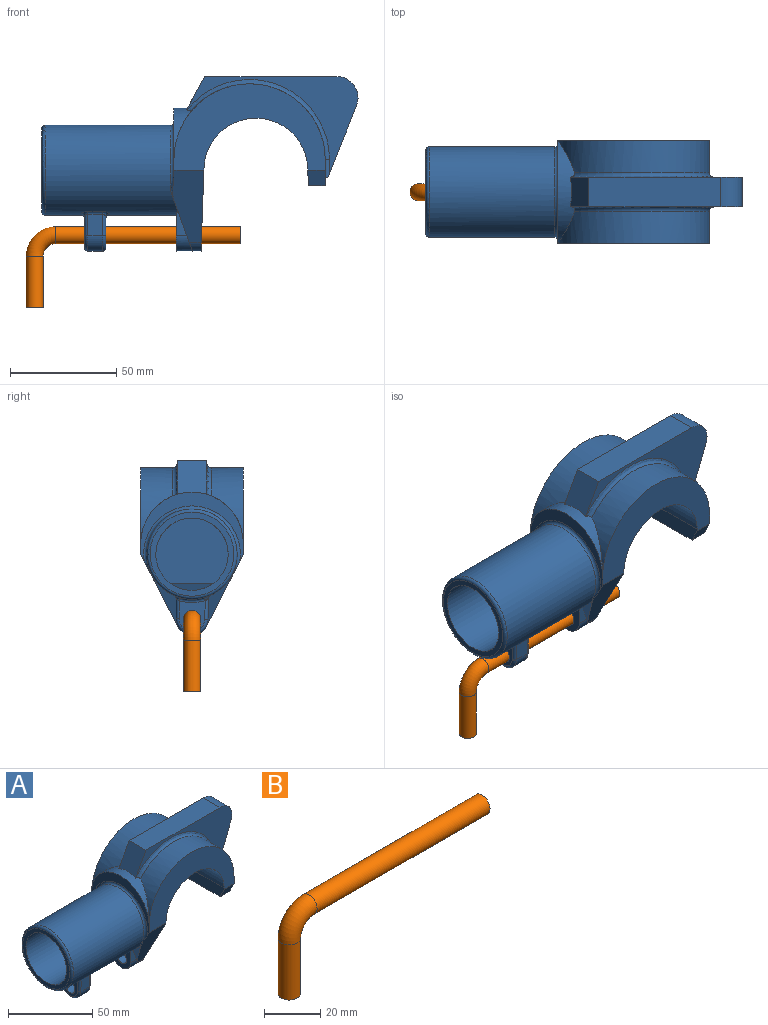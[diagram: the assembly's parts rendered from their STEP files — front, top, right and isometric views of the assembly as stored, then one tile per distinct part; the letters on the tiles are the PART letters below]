
ASSEMBLY  parts=2 mates=1
PART A: 63 faces, bbox 148.7x49.3x86 mm
  f0: cylinder r=21.2mm len=62.62mm, axis (1,0,0), area 7740.6mm2, adj f1,f2,f41,f43,f44,f46,f47,f49
  f1: plane 24.1x12.21mm, normal (-0.94,0,-0.34), area 61.4mm2, adj f0,f15,f54,f58,f60
  f2: plane 28.33x18.79mm, normal (-0.94,0,-0.34), area 63.1mm2, adj f0,f14,f16,f54,f59,f60
  f3: cylinder r=35.53mm len=71.06mm, axis (0,1,0), area 1428.5mm2, adj f5,f12,f27,f29
  f4: cylinder r=35.53mm len=71.06mm, axis (0,1,0), area 1428.5mm2, adj f5,f10,f25,f29
  f5: plane 48.2x12.36mm, normal (1,0,0), area 413.2mm2, adj f3,f4,f9,f10,f12,f13,f17,f18
  f6: plane 48.2x32.34mm, normal (-1,0,0), area 350.6mm2, adj f10,f12,f14,f15,f29,f54
  f7: plane 48.2x38.85mm, normal (1,0,-0.03), area 1125.1mm2, adj f10,f11,f12,f14,f15,f16
  f8: plane 48.2x8.16mm, normal (-1,0,-0.03), area 366.3mm2, adj f9,f10,f11,f12,f13,f17
  f9: plane 40.72x7.92mm, normal (0,0,-1), area 322.5mm2, adj f5,f8,f13,f17
  f10: plane 71.06x40.61mm, normal (0,1,0), area 1407.3mm2, adj f4,f5,f6,f7,f8,f11,f13,f14
  f11: cylinder r=24.4mm len=48.77mm, axis (0,1,0), area 3612.7mm2, adj f7,f8,f10,f12
  f12: plane 71.06x40.61mm, normal (0,-1,0), area 1407.3mm2, adj f3,f5,f6,f7,f8,f11,f15,f17
  f13: plane 8.17x7.28mm, normal (0,0.89,-0.46), area 65.8mm2, adj f5,f8,f9,f10
  f14: plane 33.9x17.43mm, normal (0,0.89,-0.46), area 436.6mm2, adj f2,f6,f7,f10,f16,f54
  f15: plane 33.9x17.43mm, normal (0,-0.89,-0.46), area 436.6mm2, adj f1,f6,f7,f12,f16,f54,f56
  f16: cylinder r=7.5mm len=13.34mm, axis (1,0,0), area 75mm2, adj f2,f7,f14,f15,f56
  f17: plane 8.17x7.28mm, normal (0,-0.89,-0.46), area 65.8mm2, adj f5,f8,f9,f12
  f18: plane 18x1.21mm, normal (0,0,-1), area 18.6mm2, adj f5,f19,f26,f28
  f19: plane 33.92x14.37mm, normal (0.93,0,-0.37), area 510.7mm2, adj f18,f20,f23,f24,f26,f28
  f20: cylinder r=10mm len=14mm, axis (0,1,0), area 273mm2, adj f19,f21,f23,f24
  f21: plane 62x14mm, normal (0,0,1), area 868mm2, adj f20,f22,f23,f24
  f22: plane 15.89x14mm, normal (-0.88,0,0.48), area 242.4mm2, adj f21,f23,f24,f29
  f23: plane 80.68x45.59mm, normal (0,-1,0), area 824.3mm2, adj f19,f20,f21,f22,f27,f28,f29
  f24: plane 80.68x45.59mm, normal (0,1,0), area 824.3mm2, adj f19,f20,f21,f22,f25,f26,f29
  f25: torus R=37.53mm, axis (0,-1,0), area 280.3mm2, adj f4,f24,f26,f29
  f26: cylinder r=2mm len=8.62mm, axis (0,0,-1), area 26.3mm2, adj f5,f18,f19,f24,f25
  f27: torus R=37.53mm, axis (0,-1,0), area 280.3mm2, adj f3,f23,f28,f29
  f28: cylinder r=2mm len=8.62mm, axis (0,0,1), area 26.3mm2, adj f5,f18,f19,f23,f27
  f29: cylinder r=24.1mm len=48.2mm, axis (-1,0,0), area 298.9mm2, adj f3,f4,f6,f22,f23,f24,f25,f27
  f30: cylinder r=17mm len=63.09mm, axis (1,0,0), area 6637.3mm2, adj f31,f32,f33
  f31: plane 39.4x39.4mm, normal (-1,0,0), area 311.3mm2, adj f30,f55
  f32: plane 19.29x3mm, normal (-0.94,0,-0.34), area 41.8mm2, adj f30,f33
  f33: plane 34x31mm, normal (-1,0,0), area 868.6mm2, adj f30,f32
  f34: plane 9.13x7mm, normal (0,1,0), area 63.9mm2, adj f35,f45,f50,f53
  f35: cylinder r=7.5mm len=15mm, axis (1,0,0), area 167.4mm2, adj f34,f37,f42,f51
  f36: cylinder r=4.05mm len=10mm, axis (1,0,0), area 254.5mm2, adj f38,f39
  f37: plane 9.97x7mm, normal (0,-1,-0.02), area 69.8mm2, adj f35,f40,f43,f48
  f38: plane 14.66x12.2mm, normal (-1,0,0), area 102.6mm2, adj f36,f40,f42,f44,f45
  f39: plane 14.66x12.2mm, normal (1,0,0), area 102.6mm2, adj f36,f48,f49,f51,f53
  f40: cylinder r=1.5mm len=10.01mm, axis (0,0.02,-1), area 22.4mm2, adj f37,f38,f41,f42
  f41: bspline ~3.18x2.99mm, area 6.8mm2, adj f0,f40,f43,f44
  f42: torus R=6mm, axis (-1,0,0), area 52.3mm2, adj f35,f38,f40,f45
  f43: cylinder r=1.5mm len=7mm, axis (1,0,0), area 11.9mm2, adj f0,f37,f41,f46
  f44: torus R=22.7mm, axis (-1,0,0), area 27.8mm2, adj f0,f38,f41,f47
  f45: cylinder r=1.5mm len=9.19mm, axis (0,0,1), area 20.6mm2, adj f34,f38,f42,f47
  f46: bspline ~3.62x3.18mm, area 6.8mm2, adj f0,f43,f48,f49
  f47: bspline ~3.62x3.17mm, area 6.8mm2, adj f0,f44,f45,f50
  f48: cylinder r=1.5mm len=10.01mm, axis (0,-0.02,1), area 22.4mm2, adj f37,f39,f46,f51
  f49: torus R=22.7mm, axis (-1,0,0), area 27.8mm2, adj f0,f39,f46,f52
  f50: cylinder r=1.5mm len=7mm, axis (1,0,0), area 12.2mm2, adj f0,f34,f47,f52
  f51: torus R=6mm, axis (-1,0,0), area 52.3mm2, adj f35,f39,f48,f53
  f52: bspline ~3.62x3.44mm, area 6.8mm2, adj f0,f49,f50,f53
  f53: cylinder r=1.5mm len=9.19mm, axis (0,0,-1), area 20.6mm2, adj f34,f39,f51,f52
  f54: torus R=22.7mm, axis (1,0,0), area 198.7mm2, adj f0,f1,f2,f6,f14,f15
  f55: torus R=19.7mm, axis (-1,0,0), area 305.8mm2, adj f0,f31
  f56: plane 6.93x4.23mm, normal (0.94,0,0.34), area 0mm2, adj f15,f16,f60
  f57: plane 18.27x15.25mm, normal (-1,0,0), area 184.3mm2, adj f0,f58,f59,f60,f61
  f58: plane 10.94x5.06mm, normal (0,-1,-0.02), area 33.6mm2, adj f0,f1,f57,f60
  f59: plane 10.14x4.81mm, normal (0,1,0), area 30.1mm2, adj f0,f2,f57,f60
  f60: cylinder r=7.5mm len=15mm, axis (-1,0,0), area 160.4mm2, adj f1,f2,f56,f57,f58,f59
  f61: cylinder r=4.05mm len=8.1mm, axis (-1,0,0), area 127.2mm2, adj f57,f62
  f62: plane 8.1x8.1mm, normal (-0.94,0,-0.34), area 54.8mm2, adj f61
PART B: 5 faces, bbox 102.2x8x39.2 mm
  f0: plane 8x8mm, normal (0,0,-1), area 50.3mm2, adj f2
  f1: plane 8x8mm, normal (1,0,0), area 50.3mm2, adj f4
  f2: cylinder r=4mm len=24mm, axis (0,0,1), area 603.2mm2, adj f0,f3
  f3: torus R=10mm, axis (0,1,0), area 394.8mm2, adj f2,f4
  f4: cylinder r=4mm len=87mm, axis (1,0,0), area 2186.5mm2, adj f1,f3
PLACE A t=(29.08,-9.78,-20.13)mm fixed
PLACE B t=(-74.89,-9.78,-84.63)mm
MATE fastened B.f4 <-> A.f60  axis (1,0,0) through (-21.39,-9.78,-50.63)mm
